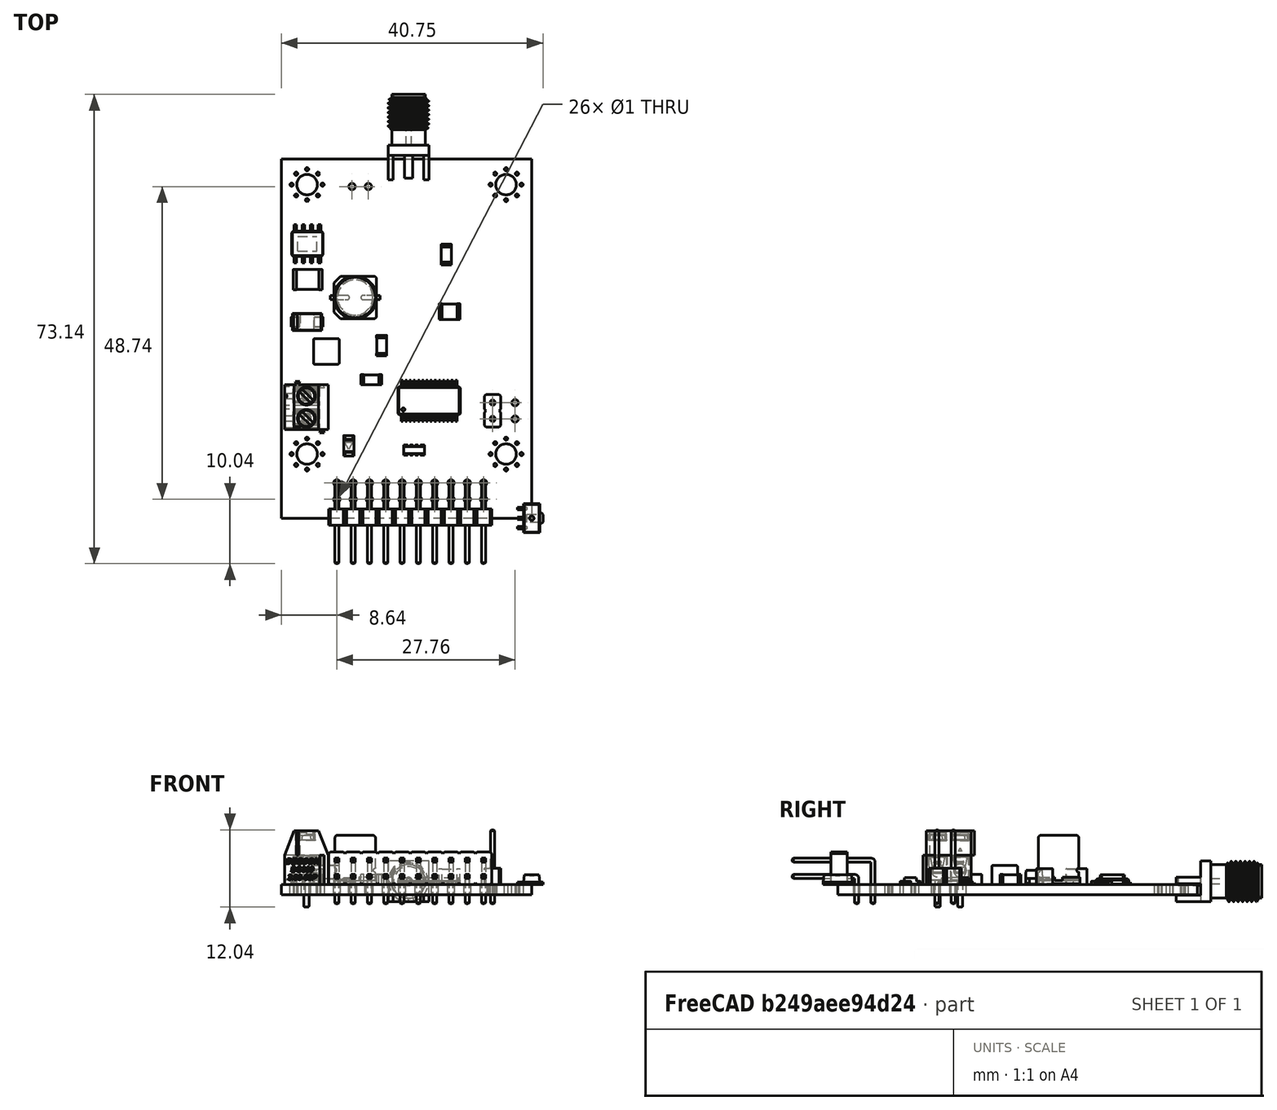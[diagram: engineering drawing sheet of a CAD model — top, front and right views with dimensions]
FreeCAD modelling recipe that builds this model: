
FCSTD DOCUMENT  (FreeCAD 1.0R39109 (Git))
Label: dac
License: All rights reserved
LicenseURL: https://en.wikipedia.org/wiki/All_rights_reserved
objects: App::Link×47, Part::Feature×22, App::Part×10, PartDesign::CoordinateSystem×1, Sketcher::SketchObject×1
note: 25 computed .brp shape members not serialized (recipe doc carries the construction recipe); baked Part::Feature solids carry a one-line shape summary decoded from their .brp

FEATURE [PartDesign::CoordinateSystem] Local_CS_2375
  AttacherType = Attacher::AttachEngine3D
  MapMode = 2
FEATURE [Part::Feature] Pcb_2375
  Placement = pos=(-126.3,128.5,0) rot=(0,0,1;0rad)
  shape: bbox 39 x 56 x 1.6 mm, 70 faces (baked)
FEATURE [Sketcher::SketchObject] PCB_Sketch_2375
  ArcFitTolerance = 1e-06
  FullyConstrained = false
  MakeInternals = false
  sketch-geometry (4):
    g0: LineSegment StartX=-39 StartY=56 StartZ=0 EndX=0 EndY=56 EndZ=0
    g1: LineSegment StartX=0 StartY=56 StartZ=0 EndX=0 EndY=0 EndZ=0
    g2: LineSegment StartX=0 StartY=0 StartZ=0 EndX=-39 EndY=0 EndZ=0
    g3: LineSegment StartX=-39 StartY=0 StartZ=0 EndX=-39 EndY=56 EndZ=0
  constraints (4):
    c: Coincident(g2,g3)
    c: Coincident(g0,g3)
    c: Coincident(g1,g2)
    c: Coincident(g0,g1)
FEATURE [App::Part] Board_Geoms_2375
  Group = -> [Pcb_2375,PCB_Sketch_2375]
  Origin = -> Origin
FEATURE [Part::Feature] Shape  label="REF_TSSOP_28_44x97mm_P065mm_c3a42edb85d4"
  Placement = pos=(-16,18.3,0) rot=(0,0,1;1.5708rad)
  shape: bbox 9.7 x 6.4 x 1.1 mm, 456 faces (baked)
FEATURE [Part::Feature] Shape001  label="REF_R_1206_3216Metric_dea5eb461704"
  Placement = pos=(-13.3,41.1,0) rot=(0,0,1;1.5708rad)
  shape: bbox 1.6 x 3.2 x 0.55 mm, 26 faces (baked)
FEATURE [Part::Feature] Shape002  label="REF_L_1206_3216Metric_923911bd139e"
  Placement = pos=(-23.4,26.9,0) rot=(0,0,1;1.5708rad)
  shape: bbox 1.6 x 3.2 x 1.6 mm, 28 faces (baked)
FEATURE [Part::Feature] Shape003  label="REF_R_Array_Convex_4x0603_e66b4cefd16a"
  Placement = pos=(-18.3333,10.6,0) rot=(0,0,1;1.5708rad)
  shape: bbox 3.2 x 1.6 x 0.5 mm, 206 faces (baked)
FEATURE [Part::Feature] Shape004  label="REF_C_1812_4532Metric_fd35fdb9ec24"
  Placement = pos=(-34.9,37.2,0) rot=(0,0,1;0rad)
  shape: bbox 4.5 x 3.2 x 2.5 mm, 28 faces (baked)
FEATURE [Part::Feature] Shape005  label="REF_CP_Elec_63x77_0427d7c4acbc"
  Placement = pos=(-27.5,34.4,0) rot=(0,0,1;0rad)
  shape: bbox 8.606 x 8.603 x 7.7 mm, 41 faces (baked)
FEATURE [Part::Feature] Shape006  label="REF_D_SMA_bc62c40d3f1a"
  Placement = pos=(-35,30.6,0) rot=(0,0,1;0rad)
  shape: bbox 5 x 2.7 x 2.22 mm, 41 faces (baked)
FEATURE [App::Link] REF_R_Array_Convex_4x0603_e66b4cefd16a_ln_  label="REF_REF_R_Array_Convex_4x0603_60d2f3ed0a64"
  LinkPlacement = pos=(-14.1667,10.6,0) rot=(0,0,1;1.5708rad)
  LinkedObject = -> Shape003
  Placement = pos=(-14.1667,10.6,0) rot=(0,0,1;1.5708rad)
FEATURE [App::Link] REF_L_1206_3216Metric_923911bd139e_ln_  label="REF_REF_L_1206_3216Metric_92d995cbed52"
  LinkPlacement = pos=(-25.7,26.9,0) rot=(0,0,1;1.5708rad)
  LinkedObject = -> Shape002
  Placement = pos=(-25.7,26.9,0) rot=(0,0,1;1.5708rad)
FEATURE [Part::Feature] Shape007  label="REF_C_1206_3216Metric_ecc4e7f1350d"
  Placement = pos=(-25,21.6,0) rot=(0,0,1;3.14159rad)
  shape: bbox 3.2 x 1.6 x 1.6 mm, 28 faces (baked)
FEATURE [App::Link] REF_C_1206_3216Metric_ecc4e7f1350d_ln_  label="REF_REF_C_1206_3216Metric_d5ebf2718203"
  LinkPlacement = pos=(-9.4,26.9,0) rot=(0,0,1;1.5708rad)
  LinkedObject = -> Shape007
  Placement = pos=(-9.4,26.9,0) rot=(0,0,1;1.5708rad)
FEATURE [Part::Feature] Shape008  label="REF_PinHeader_2x10_P254mm_Horizontal_c3ac748f6938"
  Placement = pos=(-7.5,5.5,0) rot=(0,0,-1;1.5708rad)
  shape: bbox 25.4 x 12.9 x 8.08 mm, 484 faces (baked)
FEATURE [Part::Feature] Shape009  label="REF_PinHeader_1x02_P254mm_Vertical_c2c35adffc7d"
  Placement = pos=(-6.1,18,0) rot=(0,0,1;0rad)
  shape: bbox 2.54 x 5.08 x 11.54 mm, 52 faces (baked)
FEATURE [Part::Feature] Part__Feature  label="adbeea57-9c39-11ed-93f0-dde97e994e83_part"
  shape: bbox 2.5 x 4.5 x 1.5 mm, 12 faces (baked)
FEATURE [App::Part] adbeea57_9c39_11ed_93f0_dde97e994e83  label="adbeea57-9c39-11ed-93f0-dde97e994e83"
  Group = -> [Part__Feature]
  Origin = -> Origin008
FEATURE [Part::Feature] Part__Feature001  label="adbeea58-9c39-11ed-93f0-dde97e994e83_part"
  shape: bbox 2.5 x 1.6 x 0.4 mm, 12 faces (baked)
FEATURE [App::Part] adbeea58_9c39_11ed_93f0_dde97e994e83  label="adbeea58-9c39-11ed-93f0-dde97e994e83"
  Group = -> [Part__Feature001]
  Origin = -> Origin009
FEATURE [Part::Feature] Part__Feature002  label="adbeea59-9c39-11ed-93f0-dde97e994e83_part"
  shape: bbox 1.5 x 0.4 x 0.4 mm, 6 faces (baked)
FEATURE [Part::Feature] Part__Feature003  label="adbeea59-9c39-11ed-93f0-dde97e994e83_part001"
  shape: bbox 1.5 x 0.4 x 0.4 mm, 6 faces (baked)
FEATURE [Part::Feature] Part__Feature004  label="adbeea59-9c39-11ed-93f0-dde97e994e83_part002"
  shape: bbox 1.5 x 0.4 x 0.4 mm, 6 faces (baked)
FEATURE [App::Part] adbeea59_9c39_11ed_93f0_dde97e994e83_part  label="adbeea59-9c39-11ed-93f0-dde97e994e83_part003"
  Group = -> [Part__Feature002,Part__Feature003,Part__Feature004]
  Origin = -> Origin010
FEATURE [App::Part] adbeea59_9c39_11ed_93f0_dde97e994e83  label="adbeea59-9c39-11ed-93f0-dde97e994e83"
  Group = -> [adbeea59_9c39_11ed_93f0_dde97e994e83_part]
  Origin = -> Origin011
FEATURE [App::Part] adbeea56_9c39_11ed_93f0_dde97e994e83  label="adbeea56-9c39-11ed-93f0-dde97e994e83"
  Group = -> [adbeea57_9c39_11ed_93f0_dde97e994e83,adbeea58_9c39_11ed_93f0_dde97e994e83,adbeea59_9c39_11ed_93f0_dde97e994e83]
  Origin = -> Origin012
FEATURE [App::Part] CQ_assembly  label="REF_CQ assembly_e2316aff6ff6"
  Group = -> [adbeea56_9c39_11ed_93f0_dde97e994e83]
  Origin = -> Origin013
  Placement = pos=(-25.6,18.4,0) rot=(0,0,1;3.14159rad)
FEATURE [App::Link] REF_PinHeader_1x02_P254mm_Vertical_c2c35adffc7d_ln_  label="REF_REF_PinHeader_1x02_P254mm_Vertical_8d209ac5472d"
  LinkPlacement = pos=(-28,51.7,0) rot=(0,0,1;1.5708rad)
  LinkedObject = -> Shape009
  Placement = pos=(-28,51.7,0) rot=(0,0,1;1.5708rad)
FEATURE [App::Link] REF_R_1206_3216Metric_dea5eb461704_ln_  label="REF_REF_R_1206_3216Metric_28bc4882b059"
  LinkPlacement = pos=(-15.7,41.2,0) rot=(0,0,1;1.5708rad)
  LinkedObject = -> Shape001
  Placement = pos=(-15.7,41.2,0) rot=(0,0,1;1.5708rad)
FEATURE [App::Link] REF_C_1206_3216Metric_ecc4e7f1350d_ln_001  label="REF_REF_C_1206_3216Metric_9cc814834820"
  LinkPlacement = pos=(-18.7,26.9,0) rot=(0,0,1;1.5708rad)
  LinkedObject = -> Shape007
  Placement = pos=(-18.7,26.9,0) rot=(0,0,1;1.5708rad)
FEATURE [App::Link] REF_C_1206_3216Metric_ecc4e7f1350d_ln_002  label="REF_REF_C_1206_3216Metric_140ac1610760"
  LinkPlacement = pos=(-4.6,41.2,0) rot=(0,0,1;1.5708rad)
  LinkedObject = -> Shape007
  Placement = pos=(-4.6,41.2,0) rot=(0,0,1;1.5708rad)
FEATURE [Part::Feature] Shape010  label="REF_L_Cenker_CKCS4030_d8273a953477"
  Placement = pos=(-32,26,0) rot=(0,0,1;1.5708rad)
  shape: bbox 4 x 4.02 x 3 mm, 28 faces (baked)
FEATURE [App::Link] REF_C_1206_3216Metric_ecc4e7f1350d_ln_003  label="REF_REF_C_1206_3216Metric_1bdc9c04c953"
  LinkPlacement = pos=(-28.1,26.9,0) rot=(0,0,1;1.5708rad)
  LinkedObject = -> Shape007
  Placement = pos=(-28.1,26.9,0) rot=(0,0,1;1.5708rad)
FEATURE [App::Link] REF_C_1206_3216Metric_ecc4e7f1350d_ln_004  label="REF_REF_C_1206_3216Metric_cb06a00eb6bb"
  LinkPlacement = pos=(-14.1,26.9,0) rot=(0,0,1;1.5708rad)
  LinkedObject = -> Shape007
  Placement = pos=(-14.1,26.9,0) rot=(0,0,1;1.5708rad)
FEATURE [App::Link] REF_C_1206_3216Metric_ecc4e7f1350d_ln_005  label="REF_REF_C_1206_3216Metric_edc837841e0f"
  LinkPlacement = pos=(-14.5,36,0) rot=(0,0,1;1.5708rad)
  LinkedObject = -> Shape007
  Placement = pos=(-14.5,36,0) rot=(0,0,1;1.5708rad)
FEATURE [App::Link] REF_C_1206_3216Metric_ecc4e7f1350d_ln_006  label="REF_REF_C_1206_3216Metric_872d7316da85"
  LinkPlacement = pos=(-11.8,36,0) rot=(0,0,1;1.5708rad)
  LinkedObject = -> Shape007
  Placement = pos=(-11.8,36,0) rot=(0,0,1;1.5708rad)
FEATURE [App::Link] REF_C_1206_3216Metric_ecc4e7f1350d_ln_007  label="REF_REF_C_1206_3216Metric_fa080edd5de2"
  LinkPlacement = pos=(-34.7,33.7,0) rot=(0,0,1;3.14159rad)
  LinkedObject = -> Shape007
  Placement = pos=(-34.7,33.7,0) rot=(0,0,1;3.14159rad)
FEATURE [App::Link] REF_R_1206_3216Metric_dea5eb461704_ln_001  label="REF_REF_R_1206_3216Metric_daaedf7f6707"
  LinkPlacement = pos=(-7,26.9,0) rot=(0,0,1;1.5708rad)
  LinkedObject = -> Shape001
  Placement = pos=(-7,26.9,0) rot=(0,0,1;1.5708rad)
FEATURE [App::Link] REF_R_1206_3216Metric_dea5eb461704_ln_002  label="REF_REF_R_1206_3216Metric_e0c93ad1cb2a"
  LinkPlacement = pos=(-15.7,45.2,0) rot=(0,0,1;1.5708rad)
  LinkedObject = -> Shape001
  Placement = pos=(-15.7,45.2,0) rot=(0,0,1;1.5708rad)
FEATURE [Part::Feature] Shape011  label="REF_L_1210_3225Metric_5d334701bb60"
  Placement = pos=(-12.8,32.2,0) rot=(0,0,1;0rad)
  shape: bbox 3.2 x 2.5 x 2.5 mm, 28 faces (baked)
FEATURE [App::Link] REF_R_Array_Convex_4x0603_e66b4cefd16a_ln_001  label="REF_REF_R_Array_Convex_4x0603_f7815705a583"
  LinkPlacement = pos=(-22.5,10.6,0) rot=(0,0,1;1.5708rad)
  LinkedObject = -> Shape003
  Placement = pos=(-22.5,10.6,0) rot=(0,0,1;1.5708rad)
FEATURE [App::Link] REF_C_1206_3216Metric_ecc4e7f1350d_ln_008  label="REF_REF_C_1206_3216Metric_7a416d868406"
  LinkPlacement = pos=(-26.5,48.5,0) rot=(0,0,1;3.14159rad)
  LinkedObject = -> Shape007
  Placement = pos=(-26.5,48.5,0) rot=(0,0,1;3.14159rad)
FEATURE [App::Link] REF_L_1210_3225Metric_5d334701bb60_ln_  label="REF_REF_L_1210_3225Metric_272e2f4baf41"
  LinkPlacement = pos=(-17,32.2,0) rot=(0,0,1;0rad)
  LinkedObject = -> Shape011
  Placement = pos=(-17,32.2,0) rot=(0,0,1;0rad)
FEATURE [App::Link] REF_R_1206_3216Metric_dea5eb461704_ln_003  label="REF_REF_R_1206_3216Metric_4bb3a19c4e52"
  LinkPlacement = pos=(-22.1,36,0) rot=(0,0,1;1.5708rad)
  LinkedObject = -> Shape001
  Placement = pos=(-22.1,36,0) rot=(0,0,1;1.5708rad)
FEATURE [App::Link] REF_PinHeader_1x02_P254mm_Vertical_c2c35adffc7d_ln_001  label="REF_REF_PinHeader_1x02_P254mm_Vertical_c0119e070db1"
  LinkPlacement = pos=(-2.6,18,0) rot=(0,0,1;0rad)
  LinkedObject = -> Shape009
  Placement = pos=(-2.6,18,0) rot=(0,0,1;0rad)
FEATURE [Part::Feature] Shape012  label="REF_SOIC-8-1EP_3.9x4.9mm_P1.27mm_EP2.29x3mm_2a411558dc4c"
  Placement = pos=(-34.95,42.77,0) rot=(0,0,1;1.5708rad)
  shape: bbox 4.9 x 6 x 1.55 mm, 152 faces (baked)
FEATURE [App::Link] REF_L_1206_3216Metric_923911bd139e_ln_001  label="REF_REF_L_1206_3216Metric_39378e988feb"
  LinkPlacement = pos=(-21.2,26.9,0) rot=(0,0,1;1.5708rad)
  LinkedObject = -> Shape002
  Placement = pos=(-21.2,26.9,0) rot=(0,0,1;1.5708rad)
FEATURE [App::Link] REF_C_1812_4532Metric_fd35fdb9ec24_ln_  label="REF_REF_C_1812_4532Metric_d066acd0d603"
  LinkPlacement = pos=(-36.5,25.9,0) rot=(0,0,1;1.5708rad)
  LinkedObject = -> Shape004
  Placement = pos=(-36.5,25.9,0) rot=(0,0,1;1.5708rad)
FEATURE [App::Link] REF_L_1210_3225Metric_5d334701bb60_ln_001  label="REF_REF_L_1210_3225Metric_7fdfb9fc9615"
  LinkPlacement = pos=(-21.3,32.2,0) rot=(0,0,1;0rad)
  LinkedObject = -> Shape011
  Placement = pos=(-21.3,32.2,0) rot=(0,0,1;0rad)
FEATURE [App::Link] REF_R_1206_3216Metric_dea5eb461704_ln_004  label="REF_REF_R_1206_3216Metric_3d4d2a619084"
  LinkPlacement = pos=(-19,49.3,0) rot=(0,0,1;1.5708rad)
  LinkedObject = -> Shape001
  Placement = pos=(-19,49.3,0) rot=(0,0,1;1.5708rad)
FEATURE [App::Link] REF_C_1206_3216Metric_ecc4e7f1350d_ln_009  label="REF_REF_C_1206_3216Metric_46c0f67f32fe"
  LinkPlacement = pos=(-14.3,48.5,0) rot=(0,0,1;3.14159rad)
  LinkedObject = -> Shape007
  Placement = pos=(-14.3,48.5,0) rot=(0,0,1;3.14159rad)
FEATURE [App::Link] REF_R_1206_3216Metric_dea5eb461704_ln_005  label="REF_REF_R_1206_3216Metric_589fc75ea92f"
  LinkPlacement = pos=(-4.7,31.3,0) rot=(0,0,1;1.5708rad)
  LinkedObject = -> Shape001
  Placement = pos=(-4.7,31.3,0) rot=(0,0,1;1.5708rad)
FEATURE [App::Link] REF_SOIC_8_1EP_3_9x4_9mm_P1_27mm_EP2_29x3mm_2a411558dc4c_ln_  label="REF_REF_SOIC-8-1EP_3.9x4.9mm_P1.27mm_EP2.29x3mm_327c7d781933"
  LinkPlacement = pos=(-8.65,42.77,0) rot=(0,0,1;1.5708rad)
  LinkedObject = -> Shape012
  Placement = pos=(-8.65,42.77,0) rot=(0,0,1;1.5708rad)
FEATURE [App::Link] REF_R_1206_3216Metric_dea5eb461704_ln_006  label="REF_REF_R_1206_3216Metric_e1e13a756e31"
  LinkPlacement = pos=(-9.5,31.4,0) rot=(0,0,1;1.5708rad)
  LinkedObject = -> Shape001
  Placement = pos=(-9.5,31.4,0) rot=(0,0,1;1.5708rad)
FEATURE [App::Link] REF_C_1206_3216Metric_ecc4e7f1350d_ln_010  label="REF_REF_C_1206_3216Metric_d8d913f8484a"
  LinkPlacement = pos=(-11.8,26.9,0) rot=(0,0,1;1.5708rad)
  LinkedObject = -> Shape007
  Placement = pos=(-11.8,26.9,0) rot=(0,0,1;1.5708rad)
FEATURE [App::Link] REF_R_1206_3216Metric_dea5eb461704_ln_007  label="REF_REF_R_1206_3216Metric_857049673542"
  LinkPlacement = pos=(-4.6,36,0) rot=(0,0,1;1.5708rad)
  LinkedObject = -> Shape001
  Placement = pos=(-4.6,36,0) rot=(0,0,1;1.5708rad)
FEATURE [Part::Feature] Shape013  label="REF_LED_1206_3216Metric_d22cfbdbfb4d"
  Placement = pos=(-28.5,11.3,0) rot=(0,0,1;1.5708rad)
  shape: bbox 1.6 x 3.2 x 1.1 mm, 50 faces (baked)
FEATURE [App::Link] REF_C_1206_3216Metric_ecc4e7f1350d_ln_011  label="REF_REF_C_1206_3216Metric_7f81c6af838c"
  LinkPlacement = pos=(-19.6,36,0) rot=(0,0,1;1.5708rad)
  LinkedObject = -> Shape007
  Placement = pos=(-19.6,36,0) rot=(0,0,1;1.5708rad)
FEATURE [App::Link] REF_C_1206_3216Metric_ecc4e7f1350d_ln_012  label="REF_REF_C_1206_3216Metric_c4aa7e021370"
  LinkPlacement = pos=(-13.4,45.2,0) rot=(0,0,1;1.5708rad)
  LinkedObject = -> Shape007
  Placement = pos=(-13.4,45.2,0) rot=(0,0,1;1.5708rad)
FEATURE [App::Link] REF_C_1206_3216Metric_ecc4e7f1350d_ln_013  label="REF_REF_C_1206_3216Metric_57fe54d1a34d"
  LinkPlacement = pos=(-24.2,45.1,0) rot=(0,0,1;1.5708rad)
  LinkedObject = -> Shape007
  Placement = pos=(-24.2,45.1,0) rot=(0,0,1;1.5708rad)
FEATURE [Part::Feature] Shape014  label="REF_SMA_Samtec_SMA-J-P-H-ST-EM1_EdgeMount_10ab1944b6c5"
  Placement = pos=(-19.2,54.4375,0) rot=(0,0,1;1.5708rad)
  shape: bbox 6.633 x 13.33 x 6.523 mm, 69 faces (baked)
FEATURE [App::Link] REF_R_1206_3216Metric_dea5eb461704_ln_008  label="REF_REF_R_1206_3216Metric_5fd7c2efb940"
  LinkPlacement = pos=(-7,31.3,0) rot=(0,0,1;1.5708rad)
  LinkedObject = -> Shape001
  Placement = pos=(-7,31.3,0) rot=(0,0,1;1.5708rad)
FEATURE [App::Link] REF_R_1206_3216Metric_dea5eb461704_ln_009  label="REF_REF_R_1206_3216Metric_8f214b9c0e7f"
  LinkPlacement = pos=(-9.5,36,0) rot=(0,0,1;1.5708rad)
  LinkedObject = -> Shape001
  Placement = pos=(-9.5,36,0) rot=(0,0,1;1.5708rad)
FEATURE [App::Link] REF_C_1206_3216Metric_ecc4e7f1350d_ln_014  label="REF_REF_C_1206_3216Metric_6b1bf2e510a7"
  LinkPlacement = pos=(-22.4,48.5,0) rot=(0,0,1;3.14159rad)
  LinkedObject = -> Shape007
  Placement = pos=(-22.4,48.5,0) rot=(0,0,1;3.14159rad)
FEATURE [App::Link] REF_R_1206_3216Metric_dea5eb461704_ln_010  label="REF_REF_R_1206_3216Metric_47425226c818"
  LinkPlacement = pos=(-16.3,26.9,0) rot=(0,0,1;1.5708rad)
  LinkedObject = -> Shape001
  Placement = pos=(-16.3,26.9,0) rot=(0,0,1;1.5708rad)
FEATURE [App::Link] REF_R_1206_3216Metric_dea5eb461704_ln_011  label="REF_REF_R_1206_3216Metric_96f9e62eec0e"
  LinkPlacement = pos=(-7.1,36,0) rot=(0,0,1;1.5708rad)
  LinkedObject = -> Shape001
  Placement = pos=(-7.1,36,0) rot=(0,0,1;1.5708rad)
FEATURE [App::Link] REF_R_1206_3216Metric_dea5eb461704_ln_012  label="REF_REF_R_1206_3216Metric_56ab30c5af69"
  LinkPlacement = pos=(-25.8,11,0) rot=(0,0,1;1.5708rad)
  LinkedObject = -> Shape001
  Placement = pos=(-25.8,11,0) rot=(0,0,1;1.5708rad)
FEATURE [App::Link] REF_R_Array_Convex_4x0603_e66b4cefd16a_ln_002  label="REF_REF_R_Array_Convex_4x0603_f290d0503860"
  LinkPlacement = pos=(-10,10.6,0) rot=(0,0,1;1.5708rad)
  LinkedObject = -> Shape003
  Placement = pos=(-10,10.6,0) rot=(0,0,1;1.5708rad)
FEATURE [App::Link] REF_C_1206_3216Metric_ecc4e7f1350d_ln_015  label="REF_REF_C_1206_3216Metric_dc8951aa932c"
  LinkPlacement = pos=(-24.8,14.8,0) rot=(0,0,1;3.14159rad)
  LinkedObject = -> Shape007
  Placement = pos=(-24.8,14.8,0) rot=(0,0,1;3.14159rad)
FEATURE [Part::Feature] Shape015  label="REF_DG350-3.96-02P-12-00AH_d845d113af01"
  Placement = pos=(-31.7,20.8,0) rot=(0.57735,-0.57735,-0.57735;2.0944rad)
  shape: bbox 6.8 x 8 x 11.9 mm, 434 faces (baked)
FEATURE [App::Link] REF_R_1206_3216Metric_dea5eb461704_ln_013  label="REF_REF_R_1206_3216Metric_6aedbf5a6e43"
  LinkPlacement = pos=(-24.1,41.1,0) rot=(0,0,1;1.5708rad)
  LinkedObject = -> Shape001
  Placement = pos=(-24.1,41.1,0) rot=(0,0,1;1.5708rad)
FEATURE [App::Link] REF_R_1206_3216Metric_dea5eb461704_ln_014  label="REF_REF_R_1206_3216Metric_874934694a7d"
  LinkPlacement = pos=(-4.6,26.9,0) rot=(0,0,1;1.5708rad)
  LinkedObject = -> Shape001
  Placement = pos=(-4.6,26.9,0) rot=(0,0,1;1.5708rad)
FEATURE [App::Link] REF_R_1206_3216Metric_dea5eb461704_ln_015  label="REF_REF_R_1206_3216Metric_748cbaacc74b"
  LinkPlacement = pos=(-4.6,45.6,0) rot=(0,0,1;1.5708rad)
  LinkedObject = -> Shape001
  Placement = pos=(-4.6,45.6,0) rot=(0,0,1;1.5708rad)
FEATURE [App::Link] REF_C_1206_3216Metric_ecc4e7f1350d_ln_016  label="REF_REF_C_1206_3216Metric_436c53fa4e84"
  LinkPlacement = pos=(-17,36,0) rot=(0,0,1;1.5708rad)
  LinkedObject = -> Shape007
  Placement = pos=(-17,36,0) rot=(0,0,1;1.5708rad)
FEATURE [App::Link] REF_SOIC_8_1EP_3_9x4_9mm_P1_27mm_EP2_29x3mm_2a411558dc4c_ln_001  label="REF_REF_SOIC-8-1EP_3.9x4.9mm_P1.27mm_EP2.29x3mm_3479d8ad36aa"
  LinkPlacement = pos=(-20.05,42.77,0) rot=(0,0,1;1.5708rad)
  LinkedObject = -> Shape012
  Placement = pos=(-20.05,42.77,0) rot=(0,0,1;1.5708rad)
FEATURE [App::Link] REF_L_Cenker_CKCS4030_d8273a953477_ln_  label="REF_REF_L_Cenker_CKCS4030_3209fc811b72"
  LinkPlacement = pos=(-29,43.4,0) rot=(0,0,1;1.5708rad)
  LinkedObject = -> Shape010
  Placement = pos=(-29,43.4,0) rot=(0,0,1;1.5708rad)
FEATURE [App::Link] REF_C_1206_3216Metric_ecc4e7f1350d_ln_017  label="REF_REF_C_1206_3216Metric_a79974573d3d"
  LinkPlacement = pos=(-30.9,48.4,0) rot=(0,0,1;3.14159rad)
  LinkedObject = -> Shape007
  Placement = pos=(-30.9,48.4,0) rot=(0,0,1;3.14159rad)
FEATURE [App::Part] Top_2375
  Group = -> [Shape,Shape001,Shape002,Shape003,Shape004,Shape005,Shape006,REF_R_Array_Convex_4x0603_e66b4cefd16a_ln_,REF_L_1206_3216Metric_923911bd139e_ln_,Shape007,REF_C_1206_3216Metric_ecc4e7f1350d_ln_,Shape008,Shape009,CQ_assembly,REF_PinHeader_1x02_P254mm_Vertical_c2c35adffc7d_ln_,REF_R_1206_3216Metric_dea5eb461704_ln_,REF_C_1206_3216Metric_ecc4e7f1350d_ln_001,REF_C_1206_3216Metric_ecc4e7f1350d_ln_002,+46 more]
  Origin = -> Origin003
FEATURE [App::Part] Step_Models_2375
  Group = -> [Top_2375]
  Origin = -> Origin002
FEATURE [App::Part] Board_2375  label="dac"
  Group = -> [Local_CS_2375,Board_Geoms_2375,Step_Models_2375]
  Origin = -> Origin001
